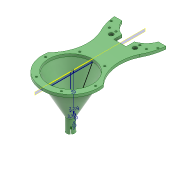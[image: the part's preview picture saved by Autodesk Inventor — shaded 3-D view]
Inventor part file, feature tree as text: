
AUTODESK INVENTOR PART (.ipt)
format: ipt  version: 2020.3 (Build 243373000, 373)  size: 259,584 bytes
history: native  units: mm
features: sketch x2, revolve x2, extrude x1, plane x1, pattern_circular x1
ambient origin geometry x8: Origin, YZ Plane, XZ Plane, XY Plane, X Axis, Y Axis, Z Axis, Center Point
bodies: Solid1 (feature_tree)
feature tree (7):
  extrude  "Extrusion1"  Depth=60.0mm TaperAngle=90.0deg
  plane  "Work Plane1"
  sketch  "Sketch3"  dims[d42=12.833071mm d43=12.833071mm d44=2.0mm d45=6.5mm d46=2.0mm d47=2.0mm d48=67.0mm d49=30.0mm d52=42.0mm d57=3.0mm d58=60.0mm d60=360.0deg d62=4.0mm d63=0.0mm d84=4.75mm d85=60.0mm d86=25.0mm d88=59.0mm d89=3.75mm d94=10.0mm d96=2.273836mm d97=90.0deg d98=10.0mm d99=17.453293mm d100=30.0mm d101=360.0deg]
  revolve  "Revolution4"  [1 undecoded]
  revolve  "Revolution5"  [1 undecoded]
  pattern_circular  "Circular Pattern3"  [2 undecoded]
  sketch  "Sketch1"  dims[d1=40.0mm d3=20.0mm d5=200.0mm d6=60.0mm d7=81.0mm d8=3.0mm d9=7.5mm d10=5.0mm d11=30.0mm d12=3.0mm d13=7.5mm d14=5.0mm d15=3.0mm d16=3.0mm d17=5.0mm d18=48.0mm d19=55.0mm d20=3.0mm d21=4.5mm d22=3.0mm d23=4.5mm d24=360.0deg d25=80.0mm d26=72.56mm d27=3.0mm d28=3.0mm d29=360.0deg d30=45.0deg d31=3.0mm d32=360.0deg d33=3.0mm d34=3.0mm d35=3.0mm d36=3.0mm d37=55.0mm d38=80.0mm d39=90.0deg]
note: 4 required parameter values undecoded (feature->parameter linkage not recoverable at this tier; creation-order binding heuristic only, values carry confidence <= 0.55)